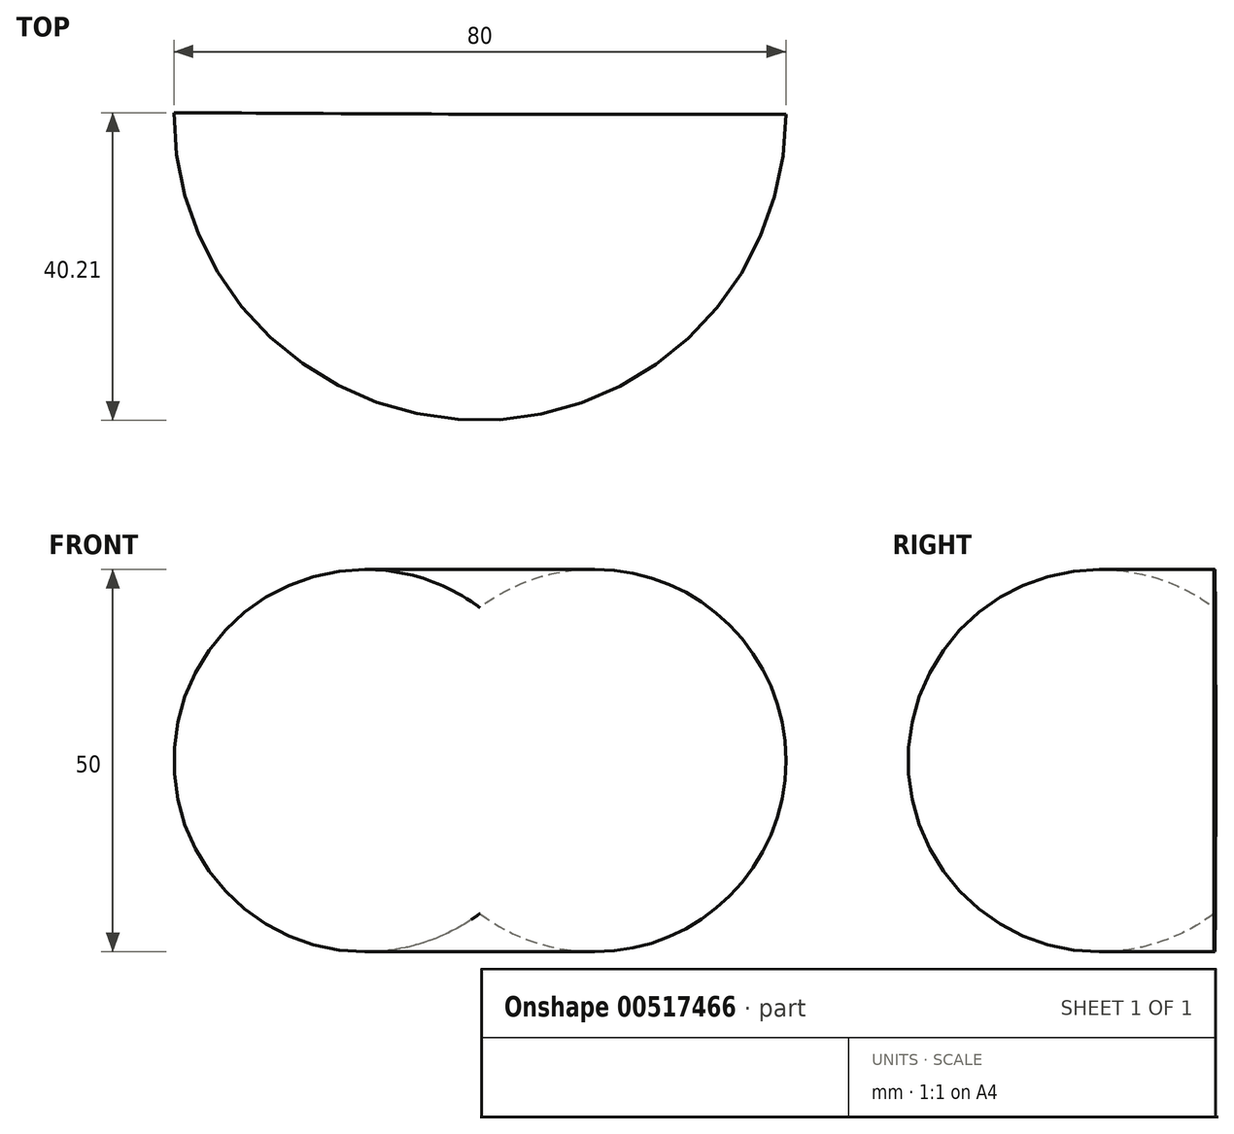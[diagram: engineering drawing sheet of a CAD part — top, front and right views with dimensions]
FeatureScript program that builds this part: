
annotation { "Feature Type Name" : "Feature", "Feature Type Description" : "" }
export const myFeature = defineFeature(function(context is Context, id is Id, definition is map)
    precondition{}
    {
        {
            var Q0;
            Q0=qCreatedBy(makeId("Front.planeOp"),FACE);
            var sketch = newSketch(context, id + "F0", { "sketchPlane" : qUnion([Q0])});
            skLineSegment(sketch, "E0", {"start": v(0, 0) * mm, "end": v(0, 40) * mm});
            skArc(sketch, "E1", {"start": v(0, 40) * mm, "mid": v(-40, 20) * mm, "end": v(0, 0) * mm});
            skArc(sketch, "E2", {"start": v(0, 0) * mm, "mid": v(40, 20) * mm, "end": v(0, 40) * mm});
            skSolve(sketch);
        }
        {
            var Q0;
            Q0=makeQuery(id+"F0.imprint","IMPRINT",FACE,{"disambiguationData":[TD([[makeQuery(id+"F0.imprint","IMPRINT",EDGE,{"derivedFrom":sQuery(id+"F0.wireOp",EDGE,"E0")}),-1.0]])]});
            var Q1;
            Q1=sQuery(id+"F0.wireOp",EDGE,"E0");
            revolve(context, id + "F1", {"entities" : qUnion([Q0]), "axis" : qUnion([Q1]), "revolveType" : RevolveType.ONE_DIRECTION, "oppositeDirection" : true, "angle" : 180.3 * degree});
        }
        {
            var Q0;
            Q0=makeQuery(id+"F1.opRevolve","CAP_FACE",FACE,{"disambiguationData":[OSD([sQuery(id+"F0.wireOp",EDGE,"E0"),sQuery(id+"F0.wireOp",EDGE,"E2")])],"isStart":true});
            var sketch = newSketch(context, id + "F2", { "sketchPlane" : qUnion([Q0])});
            skFitSpline(sketch, "E3", {"points": [v(14, 35.56) * mm, v(8.57, 33.5) * mm, v(13.97, 31.77) * mm, v(9.87, 33.59) * mm, v(14, 35.56) * mm]});
            skFitSpline(sketch, "E4", {"points": [v(13.58, 27.1) * mm, v(8.93, 26.11) * mm, v(13.66, 23.87) * mm, v(10.2, 25.96) * mm, v(13.58, 27.1) * mm]});
            skFitSpline(sketch, "E5", {"points": [v(13.11, 17.8) * mm, v(8.7, 16.28) * mm, v(13.15, 14.28) * mm, v(9.58, 16.3) * mm, v(13.11, 17.8) * mm]});
            skFitSpline(sketch, "E6", {"points": [v(13.15, 7.86) * mm, v(8.3, 6.62) * mm, v(13.15, 4.18) * mm, v(9.46, 6.6) * mm, v(13.15, 7.86) * mm]});
            skFitSpline(sketch, "E7", {"points": [v(36.64, 27.69) * mm, v(36.7, 21.4) * mm, v(33.93, 24.27) * mm, v(36.64, 27.69) * mm]});
            skLineSegment(sketch, "E8", {"start": v(34.75, 26.77) * mm, "end": v(14, 35.56) * mm});
            skLineSegment(sketch, "E9", {"start": v(33.86, 24.9) * mm, "end": v(13.58, 27.1) * mm});
            skLineSegment(sketch, "E10", {"start": v(34.26, 22.66) * mm, "end": v(13.11, 17.8) * mm});
            skFitSpline(sketch, "E11", {"points": [v(-18.62, 32.41) * mm, v(-11.42, 33.93) * mm, v(-18.47, 36.17) * mm, v(-13.52, 33.9) * mm, v(-18.62, 32.41) * mm]});
            skFitSpline(sketch, "E12", {"points": [v(-18.7, 27.14) * mm, v(-11.77, 25.4) * mm, v(-19.03, 23.22) * mm, v(-13.65, 25.45) * mm, v(-18.7, 27.14) * mm]});
            skFitSpline(sketch, "E13", {"points": [v(-19.03, 18.4) * mm, v(-12.52, 16.72) * mm, v(-19.03, 14.31) * mm, v(-14, 16.65) * mm, v(-19.03, 18.4) * mm]});
            skFitSpline(sketch, "E14", {"points": [v(-18.73, 8.26) * mm, v(-12.2, 7.14) * mm, v(-18.7, 4.84) * mm, v(-13.72, 7.13) * mm, v(-18.73, 8.26) * mm]});
            skFitSpline(sketch, "E15", {"points": [v(-35.74, 25.94) * mm, v(-36.03, 17.7) * mm, v(-33.05, 21.6) * mm, v(-35.74, 25.94) * mm]});
            skLineSegment(sketch, "E16", {"start": v(-34.9, 25.94) * mm, "end": v(-18.62, 32.41) * mm});
            skLineSegment(sketch, "E17", {"start": v(-33.23, 23.55) * mm, "end": v(-19.03, 23.22) * mm});
            skLineSegment(sketch, "E18", {"start": v(-19.03, 23.22) * mm, "end": v(-33.23, 23.44) * mm});
            skLineSegment(sketch, "E19", {"start": v(-33.2, 20.24) * mm, "end": v(-19.03, 18.4) * mm});
            skLineSegment(sketch, "E20", {"start": v(36.7, 21.4) * mm, "end": v(13.15, 7.86) * mm});
            skLineSegment(sketch, "E21", {"start": v(-34.94, 17.9) * mm, "end": v(-18.66, 8.45) * mm});
            skSolve(sketch);
        }
        {
            var Q0;
            Q0=sQuery(id+"F2.wireOp",EDGE,"E6");
            var Q1;
            Q1=sQuery(id+"F2.wireOp",EDGE,"E5");
            var Q2;
            Q2=sQuery(id+"F2.wireOp",EDGE,"E3");
            var Q3;
            Q3=sQuery(id+"F2.wireOp",EDGE,"E4");
            var Q4;
            Q4=sQuery(id+"F2.wireOp",EDGE,"E13");
            var Q5;
            Q5=sQuery(id+"F2.wireOp",EDGE,"E12");
            var Q6;
            Q6=sQuery(id+"F2.wireOp",EDGE,"E14");
            var Q7;
            Q7=sQuery(id+"F2.wireOp",EDGE,"E11");
            extrude(context, id + "F3", {"bodyType" : ToolBodyType.SURFACE, "surfaceEntities" : qUnion([Q0, Q1, Q2, Q3, Q4, Q5, Q6, Q7]), "depth" : 2.5 * mm, "offsetDistance" : 25 * mm});
        }
        {
            var Q0;
            Q0=sQuery(id+"F2.wireOp",EDGE,"E15");
            var Q1;
            Q1=sQuery(id+"F2.wireOp",EDGE,"E7");
            extrude(context, id + "F4", {"bodyType" : ToolBodyType.SURFACE, "surfaceEntities" : qUnion([Q0, Q1]), "depth" : 2.5 * mm, "offsetDistance" : 25 * mm});
        }
        {
            var Q0;
            Q0=sQuery(id+"F2.wireOp",EDGE,"E21");
            var Q1;
            Q1=sQuery(id+"F2.wireOp",EDGE,"E20");
            var Q2;
            Q2=sQuery(id+"F2.wireOp",EDGE,"E17");
            var Q3;
            Q3=sQuery(id+"F2.wireOp",EDGE,"E16");
            var Q4;
            Q4=sQuery(id+"F2.wireOp",EDGE,"E8");
            var Q5;
            Q5=sQuery(id+"F2.wireOp",EDGE,"E19");
            var Q6;
            Q6=sQuery(id+"F2.wireOp",EDGE,"E9");
            var Q7;
            Q7=sQuery(id+"F2.wireOp",EDGE,"E10");
            extrude(context, id + "F5", {"bodyType" : ToolBodyType.SURFACE, "surfaceEntities" : qUnion([Q0, Q1, Q2, Q3, Q4, Q5, Q6, Q7]), "depth" : 2.5 * mm, "offsetDistance" : 25 * mm});
        }
    });
